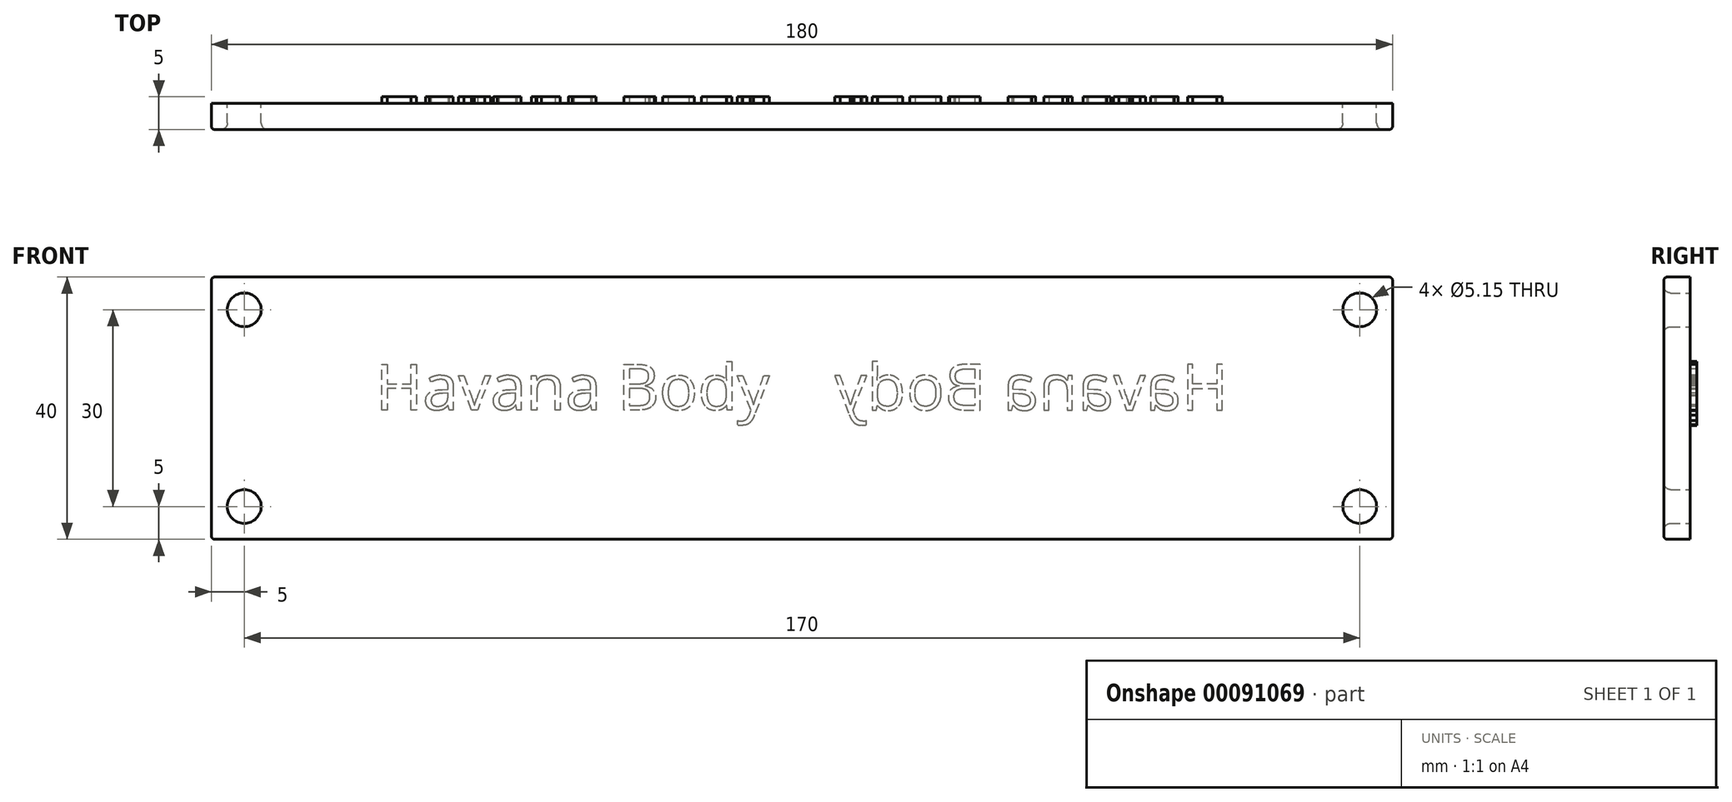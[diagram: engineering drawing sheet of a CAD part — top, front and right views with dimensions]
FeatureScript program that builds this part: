
annotation { "Feature Type Name" : "Feature", "Feature Type Description" : "" }
export const myFeature = defineFeature(function(context is Context, id is Id, definition is map)
    precondition{}
    {
        {
            var Q0;
            Q0=qCreatedBy(makeId("Front.planeOp"),FACE);
            var sketch = newSketch(context, id + "F0", { "sketchPlane" : qUnion([Q0])});
            skLineSegment(sketch, "E0.bottom", {"start": v(-90, -20) * mm, "end": v(90, -20) * mm});
            skLineSegment(sketch, "E0.top", {"start": v(-90, 20) * mm, "end": v(90, 20) * mm});
            skLineSegment(sketch, "E0.left", {"start": v(-90, -20) * mm, "end": v(-90, 20) * mm});
            skLineSegment(sketch, "E0.right", {"start": v(90, -20) * mm, "end": v(90, 20) * mm});
            skPoint(sketch, "E0.middle", {"position": v(0, 0) * mm});
            skCircle(sketch, "E1", {"center": v(-85, 15) * mm, "radius": 2.58 * mm});
            skPoint(sketch, "E2.start.orphan", {"position": v(-90, 0) * mm});
            skPoint(sketch, "E3.orphan", {"position": v(0, 20) * mm});
            skPoint(sketch, "E4.end.orphan", {"position": v(0, -20) * mm});
            skLineSegment(sketch, "E5", {"start": v(-90, 0) * mm, "end": v(0, 0) * mm, "construction": true});
            skLineSegment(sketch, "E6", {"start": v(0, 20) * mm, "end": v(0, -20) * mm, "construction": true});
            skCircle(sketch, "E7.MirrorC", {"center": v(-85, -15) * mm, "radius": 2.58 * mm});
            skCircle(sketch, "E8.MirrorC", {"center": v(85, 15) * mm, "radius": 2.58 * mm});
            skCircle(sketch, "E9.MirrorC", {"center": v(85, -15) * mm, "radius": 2.58 * mm});
            skSolve(sketch);
        }
        {
            var Q0;
            Q0=makeQuery(id+"F0.imprint","IMPRINT",FACE,{"disambiguationData":[TD([[makeQuery(id+"F0.imprint","IMPRINT",EDGE,{"derivedFrom":sQuery(id+"F0.wireOp",EDGE,"E0.bottom")}),1.0]])]});
            extrude(context, id + "F1", {"entities" : qUnion([Q0]), "depth" : 4 * mm});
        }
        {
            var Q0;
            Q0=makeQuery(id+"F1.opExtrude","CAP_EDGE",EDGE,{"disambiguationData":[OSD([sQuery(id+"F0.wireOp",EDGE,"E1")])],"isStart":false});
            var Q1;
            Q1=makeQuery(id+"F1.opExtrude","CAP_EDGE",EDGE,{"disambiguationData":[OSD([sQuery(id+"F0.wireOp",EDGE,"f5b72a5b-8583-449a-bdbf-9ac5a681e1fd0.MirrorC")])],"isStart":false});
            var Q2;
            Q2=makeQuery(id+"F1.opExtrude","CAP_EDGE",EDGE,{"disambiguationData":[OSD([sQuery(id+"F0.wireOp",EDGE,"2623e306-60f4-4522-aa65-1e3e8c2cf5b60.MirrorC")])],"isStart":false});
            var Q3;
            Q3=makeQuery(id+"F1.opExtrude","CAP_EDGE",EDGE,{"disambiguationData":[OSD([sQuery(id+"F0.wireOp",EDGE,"be81a34d-1d50-4ce7-a7a8-4484a1701fac0.MirrorC")])],"isStart":false});
            var Q4;
            Q4=makeQuery(id+"F1.opExtrude","CAP_EDGE",EDGE,{"disambiguationData":[OSD([sQuery(id+"F0.wireOp",EDGE,"E7.MirrorC")])],"isStart":false});
            var Q5;
            Q5=makeQuery(id+"F1.opExtrude","CAP_EDGE",EDGE,{"disambiguationData":[OSD([sQuery(id+"F0.wireOp",EDGE,"E8.MirrorC")])],"isStart":false});
            var Q6;
            Q6=makeQuery(id+"F1.opExtrude","CAP_EDGE",EDGE,{"disambiguationData":[OSD([sQuery(id+"F0.wireOp",EDGE,"E9.MirrorC")])],"isStart":false});
            fillet(context, id + "F2", {"entities" : qUnion([Q0, Q1, Q2, Q3, Q4, Q5, Q6]), "radius" : 1 * mm, "tangentPropagation" : true, "allowEdgeOverflow" : false});
        }
        {
            var Q0;
            Q0=makeQuery(id+"F1.opExtrude","CAP_EDGE",EDGE,{"disambiguationData":[OSD([sQuery(id+"F0.wireOp",EDGE,"E0.top")])],"isStart":false});
            var Q1;
            Q1=makeQuery(id+"F1.opExtrude","CAP_EDGE",EDGE,{"disambiguationData":[OSD([sQuery(id+"F0.wireOp",EDGE,"E0.left")])],"isStart":false});
            var Q2;
            Q2=makeQuery(id+"F1.opExtrude","CAP_EDGE",EDGE,{"disambiguationData":[OSD([sQuery(id+"F0.wireOp",EDGE,"E0.bottom")])],"isStart":false});
            var Q3;
            Q3=makeQuery(id+"F1.opExtrude","CAP_EDGE",EDGE,{"disambiguationData":[OSD([sQuery(id+"F0.wireOp",EDGE,"E0.right")])],"isStart":false});
            var Q4;
            Q4=makeQuery(id+"F1.opExtrude","SWEPT_EDGE",EDGE,{"disambiguationData":[OSD([sQuery(id+"F0.wireOp",EDGE,"E0.top"),sQuery(id+"F0.wireOp",EDGE,"E0.left")])]});
            var Q5;
            Q5=makeQuery(id+"F1.opExtrude","SWEPT_EDGE",EDGE,{"disambiguationData":[OSD([sQuery(id+"F0.wireOp",EDGE,"E0.bottom"),sQuery(id+"F0.wireOp",EDGE,"E0.left")])]});
            var Q6;
            Q6=makeQuery(id+"F1.opExtrude","SWEPT_EDGE",EDGE,{"disambiguationData":[OSD([sQuery(id+"F0.wireOp",EDGE,"E0.top"),sQuery(id+"F0.wireOp",EDGE,"E0.right")])]});
            var Q7;
            Q7=makeQuery(id+"F1.opExtrude","SWEPT_EDGE",EDGE,{"disambiguationData":[OSD([sQuery(id+"F0.wireOp",EDGE,"E0.bottom"),sQuery(id+"F0.wireOp",EDGE,"E0.right")])]});
            fillet(context, id + "F3", {"entities" : qUnion([Q0, Q1, Q2, Q3, Q4, Q5, Q6, Q7]), "radius" : .5 * mm, "tangentPropagation" : true, "allowEdgeOverflow" : false});
        }
        {
            var Q0;
            Q0=makeQuery(id+"F1.opExtrude","CAP_FACE",FACE,{"disambiguationData":[OSD([sQuery(id+"F0.wireOp",EDGE,"E0.bottom"),sQuery(id+"F0.wireOp",EDGE,"E0.top"),sQuery(id+"F0.wireOp",EDGE,"E0.left"),sQuery(id+"F0.wireOp",EDGE,"E0.right"),sQuery(id+"F0.wireOp",EDGE,"E1"),sQuery(id+"F0.wireOp",EDGE,"E7.MirrorC"),sQuery(id+"F0.wireOp",EDGE,"E8.MirrorC"),sQuery(id+"F0.wireOp",EDGE,"E9.MirrorC")])],"isStart":true});
            var sketch = newSketch(context, id + "F4", { "sketchPlane" : qUnion([Q0])});
            skText(sketch, "E10", { "text": "Havana Body", "fontName": "OpenSans-Regular.ttf"});
            skLineSegment(sketch, "E11", {"start": v(0, 20) * mm, "end": v(0, -20) * mm, "construction": true});
            const initialGuessF4  = {"E10": [-0.065, -0.00027, 1, 0, 0.00703]};
            skSetInitialGuess(sketch, initialGuessF4);
            skSolve(sketch);
        }
        {
            var Q0;
            Q0=qSketchRegion(id+"F4",true);
            extrude(context, id + "F5", {"entities" : qUnion([Q0]), "operationType" : NewBodyOperationType.ADD, "depth" : 1 * mm});
        }
        {
            var Q0;
            Q0=makeQuery(id+"F1.opExtrude","SWEPT_BODY",BODY,{"disambiguationData":[OSD([sQuery(id+"F0.wireOp",EDGE,"E0.bottom"),sQuery(id+"F0.wireOp",EDGE,"E0.top"),sQuery(id+"F0.wireOp",EDGE,"E0.left"),sQuery(id+"F0.wireOp",EDGE,"E0.right"),sQuery(id+"F0.wireOp",EDGE,"E1"),sQuery(id+"F0.wireOp",EDGE,"E7.MirrorC"),sQuery(id+"F0.wireOp",EDGE,"E8.MirrorC"),sQuery(id+"F0.wireOp",EDGE,"E9.MirrorC")])]});
            var Q1;
            Q1=makeQuery(id+"F5.opExtrude","SWEPT_FACE",FACE,{"disambiguationData":[OSD([sQuery(id+"F4.wireOp",EDGE,"E10.sketch_text.stroke-94")])]});
            var Q2;
            Q2=makeQuery(id+"F5.opExtrude","SWEPT_FACE",FACE,{"disambiguationData":[OSD([sQuery(id+"F4.wireOp",EDGE,"E10.sketch_text.stroke-169")])]});
            var Q3;
            Q3=makeQuery(id+"F5.opExtrude","SWEPT_FACE",FACE,{"disambiguationData":[OSD([sQuery(id+"F4.wireOp",EDGE,"E10.sketch_text.stroke-185")])]});
            var Q4;
            Q4=makeQuery(id+"F5.opExtrude","SWEPT_FACE",FACE,{"disambiguationData":[OSD([sQuery(id+"F4.wireOp",EDGE,"E10.sketch_text.stroke-125")])]});
            var Q5;
            Q5=makeQuery(id+"F5.opExtrude","SWEPT_FACE",FACE,{"disambiguationData":[OSD([sQuery(id+"F4.wireOp",EDGE,"E10.sketch_text.stroke-155")])]});
            var Q6;
            Q6=makeQuery(id+"F5.opExtrude","SWEPT_FACE",FACE,{"disambiguationData":[OSD([sQuery(id+"F4.wireOp",EDGE,"E10.sketch_text.stroke-65")])]});
            var Q7;
            Q7=makeQuery(id+"F5.opExtrude","SWEPT_FACE",FACE,{"disambiguationData":[OSD([sQuery(id+"F4.wireOp",EDGE,"E10.sketch_text.stroke-81")])]});
            var Q8;
            Q8=makeQuery(id+"F5.opExtrude","SWEPT_FACE",FACE,{"disambiguationData":[OSD([sQuery(id+"F4.wireOp",EDGE,"E10.sketch_text.stroke-67")])]});
            var Q9;
            Q9=makeQuery(id+"F5.opExtrude","SWEPT_FACE",FACE,{"disambiguationData":[OSD([sQuery(id+"F4.wireOp",EDGE,"E10.sketch_text.stroke-99")])]});
            var Q10;
            Q10=makeQuery(id+"F5.opExtrude","SWEPT_FACE",FACE,{"disambiguationData":[OSD([sQuery(id+"F4.wireOp",EDGE,"E10.sketch_text.stroke-127")])]});
            var Q11;
            Q11=makeQuery(id+"F5.opExtrude","SWEPT_FACE",FACE,{"disambiguationData":[OSD([sQuery(id+"F4.wireOp",EDGE,"E10.sketch_text.stroke-10")])]});
            var Q12;
            Q12=makeQuery(id+"F5.opExtrude","CAP_FACE",FACE,{"disambiguationData":[OSD([sQuery(id+"F4.wireOp",EDGE,"E10.sketch_text.stroke-9"),sQuery(id+"F4.wireOp",EDGE,"E10.sketch_text.stroke-10"),sQuery(id+"F4.wireOp",EDGE,"E10.sketch_text.stroke-11"),sQuery(id+"F4.wireOp",EDGE,"E10.sketch_text.stroke-12")])],"isStart":false});
            var Q13;
            Q13=makeQuery(id+"F5.opExtrude","SWEPT_FACE",FACE,{"disambiguationData":[OSD([sQuery(id+"F4.wireOp",EDGE,"E10.sketch_text.stroke-154")])]});
            var Q14;
            Q14=makeQuery(id+"F5.opExtrude","SWEPT_FACE",FACE,{"disambiguationData":[OSD([sQuery(id+"F4.wireOp",EDGE,"E10.sketch_text.stroke-1")])]});
            var Q15;
            Q15=makeQuery(id+"F5.opExtrude","CAP_FACE",FACE,{"disambiguationData":[OSD([sQuery(id+"F4.wireOp",EDGE,"E10.sketch_text.stroke-124"),sQuery(id+"F4.wireOp",EDGE,"E10.sketch_text.stroke-125"),sQuery(id+"F4.wireOp",EDGE,"E10.sketch_text.stroke-126"),sQuery(id+"F4.wireOp",EDGE,"E10.sketch_text.stroke-127"),sQuery(id+"F4.wireOp",EDGE,"E10.sketch_text.stroke-128"),sQuery(id+"F4.wireOp",EDGE,"E10.sketch_text.stroke-129"),sQuery(id+"F4.wireOp",EDGE,"E10.sketch_text.stroke-130"),sQuery(id+"F4.wireOp",EDGE,"E10.sketch_text.stroke-131"),sQuery(id+"F4.wireOp",EDGE,"E10.sketch_text.stroke-132"),sQuery(id+"F4.wireOp",EDGE,"E10.sketch_text.stroke-133"),sQuery(id+"F4.wireOp",EDGE,"E10.sketch_text.stroke-134"),sQuery(id+"F4.wireOp",EDGE,"E10.sketch_text.stroke-135"),sQuery(id+"F4.wireOp",EDGE,"E10.sketch_text.stroke-136"),sQuery(id+"F4.wireOp",EDGE,"E10.sketch_text.stroke-137"),sQuery(id+"F4.wireOp",EDGE,"E10.sketch_text.stroke-138")])],"isStart":false});
            var Q16;
            Q16=makeQuery(id+"F5.opExtrude","CAP_FACE",FACE,{"disambiguationData":[OSD([sQuery(id+"F4.wireOp",EDGE,"E10.sketch_text.stroke-34"),sQuery(id+"F4.wireOp",EDGE,"E10.sketch_text.stroke-35"),sQuery(id+"F4.wireOp",EDGE,"E10.sketch_text.stroke-36"),sQuery(id+"F4.wireOp",EDGE,"E10.sketch_text.stroke-37"),sQuery(id+"F4.wireOp",EDGE,"E10.sketch_text.stroke-38"),sQuery(id+"F4.wireOp",EDGE,"E10.sketch_text.stroke-39"),sQuery(id+"F4.wireOp",EDGE,"E10.sketch_text.stroke-40"),sQuery(id+"F4.wireOp",EDGE,"E10.sketch_text.stroke-41"),sQuery(id+"F4.wireOp",EDGE,"E10.sketch_text.stroke-42"),sQuery(id+"F4.wireOp",EDGE,"E10.sketch_text.stroke-43"),sQuery(id+"F4.wireOp",EDGE,"E10.sketch_text.stroke-44"),sQuery(id+"F4.wireOp",EDGE,"E10.sketch_text.stroke-45"),sQuery(id+"F4.wireOp",EDGE,"E10.sketch_text.stroke-46"),sQuery(id+"F4.wireOp",EDGE,"E10.sketch_text.stroke-47"),sQuery(id+"F4.wireOp",EDGE,"E10.sketch_text.stroke-48"),sQuery(id+"F4.wireOp",EDGE,"E10.sketch_text.stroke-49"),sQuery(id+"F4.wireOp",EDGE,"E10.sketch_text.stroke-50"),sQuery(id+"F4.wireOp",EDGE,"E10.sketch_text.stroke-51"),sQuery(id+"F4.wireOp",EDGE,"E10.sketch_text.stroke-52"),sQuery(id+"F4.wireOp",EDGE,"E10.sketch_text.stroke-53"),sQuery(id+"F4.wireOp",EDGE,"E10.sketch_text.stroke-54"),sQuery(id+"F4.wireOp",EDGE,"E10.sketch_text.stroke-55"),sQuery(id+"F4.wireOp",EDGE,"E10.sketch_text.stroke-56"),sQuery(id+"F4.wireOp",EDGE,"E10.sketch_text.stroke-57"),sQuery(id+"F4.wireOp",EDGE,"E10.sketch_text.stroke-58"),sQuery(id+"F4.wireOp",EDGE,"E10.sketch_text.stroke-59"),sQuery(id+"F4.wireOp",EDGE,"E10.sketch_text.stroke-60")])],"isStart":false});
            var Q17;
            Q17=makeQuery(id+"F5.opExtrude","SWEPT_FACE",FACE,{"disambiguationData":[OSD([sQuery(id+"F4.wireOp",EDGE,"E10.sketch_text.stroke-50")])]});
            var Q18;
            Q18=makeQuery(id+"F5.opExtrude","SWEPT_FACE",FACE,{"disambiguationData":[OSD([sQuery(id+"F4.wireOp",EDGE,"E10.sketch_text.stroke-2")])]});
            var Q19;
            Q19=makeQuery(id+"F5.opExtrude","SWEPT_FACE",FACE,{"disambiguationData":[OSD([sQuery(id+"F4.wireOp",EDGE,"E10.sketch_text.stroke-3")])]});
            var Q20;
            Q20=makeQuery(id+"F5.opExtrude","SWEPT_FACE",FACE,{"disambiguationData":[OSD([sQuery(id+"F4.wireOp",EDGE,"E10.sketch_text.stroke-5")])]});
            var Q21;
            Q21=makeQuery(id+"F5.opExtrude","SWEPT_FACE",FACE,{"disambiguationData":[OSD([sQuery(id+"F4.wireOp",EDGE,"E10.sketch_text.stroke-8")])]});
            var Q22;
            Q22=makeQuery(id+"F5.opExtrude","SWEPT_FACE",FACE,{"disambiguationData":[OSD([sQuery(id+"F4.wireOp",EDGE,"E10.sketch_text.stroke-98")])]});
            var Q23;
            Q23=makeQuery(id+"F5.opExtrude","SWEPT_FACE",FACE,{"disambiguationData":[OSD([sQuery(id+"F4.wireOp",EDGE,"E10.sketch_text.stroke-66")])]});
            var Q24;
            Q24=makeQuery(id+"F5.opExtrude","SWEPT_FACE",FACE,{"disambiguationData":[OSD([sQuery(id+"F4.wireOp",EDGE,"E10.sketch_text.stroke-153")])]});
            var Q25;
            Q25=makeQuery(id+"F5.opExtrude","SWEPT_FACE",FACE,{"disambiguationData":[OSD([sQuery(id+"F4.wireOp",EDGE,"E10.sketch_text.stroke-126")])]});
            var Q26;
            Q26=makeQuery(id+"F5.opExtrude","SWEPT_FACE",FACE,{"disambiguationData":[OSD([sQuery(id+"F4.wireOp",EDGE,"E10.sketch_text.stroke-183")])]});
            var Q27;
            Q27=makeQuery(id+"F5.opExtrude","SWEPT_FACE",FACE,{"disambiguationData":[OSD([sQuery(id+"F4.wireOp",EDGE,"E10.sketch_text.stroke-109")])]});
            var Q28;
            Q28=makeQuery(id+"F5.opExtrude","SWEPT_FACE",FACE,{"disambiguationData":[OSD([sQuery(id+"F4.wireOp",EDGE,"E10.sketch_text.stroke-186")])]});
            var Q29;
            Q29=makeQuery(id+"F5.opExtrude","SWEPT_FACE",FACE,{"disambiguationData":[OSD([sQuery(id+"F4.wireOp",EDGE,"E10.sketch_text.stroke-79")])]});
            var Q30;
            Q30=makeQuery(id+"F5.opExtrude","SWEPT_FACE",FACE,{"disambiguationData":[OSD([sQuery(id+"F4.wireOp",EDGE,"E10.sketch_text.stroke-110")])]});
            var Q31;
            Q31=makeQuery(id+"F5.opExtrude","SWEPT_FACE",FACE,{"disambiguationData":[OSD([sQuery(id+"F4.wireOp",EDGE,"E10.sketch_text.stroke-38")])]});
            var Q32;
            Q32=makeQuery(id+"F5.opExtrude","SWEPT_FACE",FACE,{"disambiguationData":[OSD([sQuery(id+"F4.wireOp",EDGE,"E10.sketch_text.stroke-24")])]});
            var Q33;
            Q33=makeQuery(id+"F5.opExtrude","SWEPT_FACE",FACE,{"disambiguationData":[OSD([sQuery(id+"F4.wireOp",EDGE,"E10.sketch_text.stroke-12")])]});
            var Q34;
            Q34=makeQuery(id+"F5.opExtrude","SWEPT_FACE",FACE,{"disambiguationData":[OSD([sQuery(id+"F4.wireOp",EDGE,"E10.sketch_text.stroke-100")])]});
            var Q35;
            Q35=makeQuery(id+"F5.opExtrude","SWEPT_FACE",FACE,{"disambiguationData":[OSD([sQuery(id+"F4.wireOp",EDGE,"E10.sketch_text.stroke-158")])]});
            var Q36;
            Q36=makeQuery(id+"F5.opExtrude","SWEPT_FACE",FACE,{"disambiguationData":[OSD([sQuery(id+"F4.wireOp",EDGE,"E10.sketch_text.stroke-142")])]});
            var Q37;
            Q37=makeQuery(id+"F5.opExtrude","SWEPT_FACE",FACE,{"disambiguationData":[OSD([sQuery(id+"F4.wireOp",EDGE,"E10.sketch_text.stroke-54")])]});
            var Q38;
            Q38=makeQuery(id+"F5.opExtrude","SWEPT_FACE",FACE,{"disambiguationData":[OSD([sQuery(id+"F4.wireOp",EDGE,"E10.sketch_text.stroke-25")])]});
            var Q39;
            Q39=makeQuery(id+"F5.opExtrude","SWEPT_FACE",FACE,{"disambiguationData":[OSD([sQuery(id+"F4.wireOp",EDGE,"E10.sketch_text.stroke-101")])]});
            var Q40;
            Q40=makeQuery(id+"F5.opExtrude","SWEPT_FACE",FACE,{"disambiguationData":[OSD([sQuery(id+"F4.wireOp",EDGE,"E10.sketch_text.stroke-69")])]});
            var Q41;
            Q41=makeQuery(id+"F5.opExtrude","SWEPT_FACE",FACE,{"disambiguationData":[OSD([sQuery(id+"F4.wireOp",EDGE,"E10.sketch_text.stroke-159")])]});
            var Q42;
            Q42=makeQuery(id+"F5.opExtrude","SWEPT_FACE",FACE,{"disambiguationData":[OSD([sQuery(id+"F4.wireOp",EDGE,"E10.sketch_text.stroke-85")])]});
            var Q43;
            Q43=makeQuery(id+"F5.opExtrude","SWEPT_FACE",FACE,{"disambiguationData":[OSD([sQuery(id+"F4.wireOp",EDGE,"E10.sketch_text.stroke-173")])]});
            var Q44;
            Q44=makeQuery(id+"F5.opExtrude","SWEPT_FACE",FACE,{"disambiguationData":[OSD([sQuery(id+"F4.wireOp",EDGE,"E10.sketch_text.stroke-40")])]});
            var Q45;
            Q45=makeQuery(id+"F5.opExtrude","SWEPT_FACE",FACE,{"disambiguationData":[OSD([sQuery(id+"F4.wireOp",EDGE,"E10.sketch_text.stroke-102")])]});
            var Q46;
            Q46=makeQuery(id+"F5.opExtrude","SWEPT_FACE",FACE,{"disambiguationData":[OSD([sQuery(id+"F4.wireOp",EDGE,"E10.sketch_text.stroke-86")])]});
            var Q47;
            Q47=makeQuery(id+"F5.opExtrude","SWEPT_FACE",FACE,{"disambiguationData":[OSD([sQuery(id+"F4.wireOp",EDGE,"E10.sketch_text.stroke-130")])]});
            var Q48;
            Q48=makeQuery(id+"F5.opExtrude","SWEPT_FACE",FACE,{"disambiguationData":[OSD([sQuery(id+"F4.wireOp",EDGE,"E10.sketch_text.stroke-103")])]});
            var Q49;
            Q49=makeQuery(id+"F5.opExtrude","SWEPT_FACE",FACE,{"disambiguationData":[OSD([sQuery(id+"F4.wireOp",EDGE,"E10.sketch_text.stroke-87")])]});
            var Q50;
            Q50=makeQuery(id+"F5.opExtrude","SWEPT_FACE",FACE,{"disambiguationData":[OSD([sQuery(id+"F4.wireOp",EDGE,"E10.sketch_text.stroke-145")])]});
            var Q51;
            Q51=makeQuery(id+"F5.opExtrude","SWEPT_FACE",FACE,{"disambiguationData":[OSD([sQuery(id+"F4.wireOp",EDGE,"E10.sketch_text.stroke-131")])]});
            var Q52;
            Q52=makeQuery(id+"F5.opExtrude","SWEPT_FACE",FACE,{"disambiguationData":[OSD([sQuery(id+"F4.wireOp",EDGE,"E10.sketch_text.stroke-28")])]});
            var Q53;
            Q53=makeQuery(id+"F5.opExtrude","SWEPT_FACE",FACE,{"disambiguationData":[OSD([sQuery(id+"F4.wireOp",EDGE,"E10.sketch_text.stroke-14")])]});
            var Q54;
            Q54=makeQuery(id+"F5.opExtrude","SWEPT_FACE",FACE,{"disambiguationData":[OSD([sQuery(id+"F4.wireOp",EDGE,"E10.sketch_text.stroke-88")])]});
            var Q55;
            Q55=makeQuery(id+"F5.opExtrude","SWEPT_FACE",FACE,{"disambiguationData":[OSD([sQuery(id+"F4.wireOp",EDGE,"E10.sketch_text.stroke-162")])]});
            var Q56;
            Q56=makeQuery(id+"F5.opExtrude","SWEPT_FACE",FACE,{"disambiguationData":[OSD([sQuery(id+"F4.wireOp",EDGE,"E10.sketch_text.stroke-176")])]});
            var Q57;
            Q57=makeQuery(id+"F5.opExtrude","SWEPT_FACE",FACE,{"disambiguationData":[OSD([sQuery(id+"F4.wireOp",EDGE,"E10.sketch_text.stroke-73")])]});
            var Q58;
            Q58=makeQuery(id+"F5.opExtrude","SWEPT_FACE",FACE,{"disambiguationData":[OSD([sQuery(id+"F4.wireOp",EDGE,"E10.sketch_text.stroke-59")])]});
            var Q59;
            Q59=makeQuery(id+"F5.opExtrude","SWEPT_FACE",FACE,{"disambiguationData":[OSD([sQuery(id+"F4.wireOp",EDGE,"E10.sketch_text.stroke-133")])]});
            var Q60;
            Q60=makeQuery(id+"F5.opExtrude","SWEPT_FACE",FACE,{"disambiguationData":[OSD([sQuery(id+"F4.wireOp",EDGE,"E10.sketch_text.stroke-119")])]});
            var Q61;
            Q61=makeQuery(id+"F5.opExtrude","SWEPT_FACE",FACE,{"disambiguationData":[OSD([sQuery(id+"F4.wireOp",EDGE,"E10.sketch_text.stroke-74")])]});
            var Q62;
            Q62=makeQuery(id+"F5.opExtrude","SWEPT_FACE",FACE,{"disambiguationData":[OSD([sQuery(id+"F4.wireOp",EDGE,"E10.sketch_text.stroke-44")])]});
            var Q63;
            Q63=makeQuery(id+"F5.opExtrude","SWEPT_FACE",FACE,{"disambiguationData":[OSD([sQuery(id+"F4.wireOp",EDGE,"E10.sketch_text.stroke-120")])]});
            var Q64;
            Q64=makeQuery(id+"F5.opExtrude","SWEPT_FACE",FACE,{"disambiguationData":[OSD([sQuery(id+"F4.wireOp",EDGE,"E10.sketch_text.stroke-90")])]});
            var Q65;
            Q65=makeQuery(id+"F5.opExtrude","SWEPT_FACE",FACE,{"disambiguationData":[OSD([sQuery(id+"F4.wireOp",EDGE,"E10.sketch_text.stroke-178")])]});
            var Q66;
            Q66=makeQuery(id+"F5.opExtrude","SWEPT_FACE",FACE,{"disambiguationData":[OSD([sQuery(id+"F4.wireOp",EDGE,"E10.sketch_text.stroke-45")])]});
            var Q67;
            Q67=makeQuery(id+"F5.opExtrude","SWEPT_FACE",FACE,{"disambiguationData":[OSD([sQuery(id+"F4.wireOp",EDGE,"E10.sketch_text.stroke-31")])]});
            var Q68;
            Q68=makeQuery(id+"F5.opExtrude","SWEPT_FACE",FACE,{"disambiguationData":[OSD([sQuery(id+"F4.wireOp",EDGE,"E10.sketch_text.stroke-135")])]});
            var Q69;
            Q69=makeQuery(id+"F5.opExtrude","SWEPT_FACE",FACE,{"disambiguationData":[OSD([sQuery(id+"F4.wireOp",EDGE,"E10.sketch_text.stroke-179")])]});
            var Q70;
            Q70=makeQuery(id+"F5.opExtrude","SWEPT_FACE",FACE,{"disambiguationData":[OSD([sQuery(id+"F4.wireOp",EDGE,"E10.sketch_text.stroke-165")])]});
            var Q71;
            Q71=makeQuery(id+"F5.opExtrude","SWEPT_FACE",FACE,{"disambiguationData":[OSD([sQuery(id+"F4.wireOp",EDGE,"E10.sketch_text.stroke-149")])]});
            var Q72;
            Q72=makeQuery(id+"F5.opExtrude","SWEPT_FACE",FACE,{"disambiguationData":[OSD([sQuery(id+"F4.wireOp",EDGE,"E10.sketch_text.stroke-136")])]});
            var Q73;
            Q73=makeQuery(id+"F5.opExtrude","SWEPT_FACE",FACE,{"disambiguationData":[OSD([sQuery(id+"F4.wireOp",EDGE,"E10.sketch_text.stroke-122")])]});
            var Q74;
            Q74=makeQuery(id+"F5.opExtrude","SWEPT_FACE",FACE,{"disambiguationData":[OSD([sQuery(id+"F4.wireOp",EDGE,"E10.sketch_text.stroke-106")])]});
            var Q75;
            Q75=makeQuery(id+"F5.opExtrude","SWEPT_FACE",FACE,{"disambiguationData":[OSD([sQuery(id+"F4.wireOp",EDGE,"E10.sketch_text.stroke-180")])]});
            var Q76;
            Q76=makeQuery(id+"F5.opExtrude","SWEPT_FACE",FACE,{"disambiguationData":[OSD([sQuery(id+"F4.wireOp",EDGE,"E10.sketch_text.stroke-166")])]});
            var Q77;
            Q77=makeQuery(id+"F5.opExtrude","SWEPT_FACE",FACE,{"disambiguationData":[OSD([sQuery(id+"F4.wireOp",EDGE,"E10.sketch_text.stroke-150")])]});
            var Q78;
            Q78=makeQuery(id+"F5.opExtrude","SWEPT_FACE",FACE,{"disambiguationData":[OSD([sQuery(id+"F4.wireOp",EDGE,"E10.sketch_text.stroke-76")])]});
            var Q79;
            Q79=makeQuery(id+"F5.opExtrude","SWEPT_FACE",FACE,{"disambiguationData":[OSD([sQuery(id+"F4.wireOp",EDGE,"E10.sketch_text.stroke-32")])]});
            var Q80;
            Q80=makeQuery(id+"F5.opExtrude","SWEPT_FACE",FACE,{"disambiguationData":[OSD([sQuery(id+"F4.wireOp",EDGE,"E10.sketch_text.stroke-181")])]});
            var Q81;
            Q81=makeQuery(id+"F5.opExtrude","SWEPT_FACE",FACE,{"disambiguationData":[OSD([sQuery(id+"F4.wireOp",EDGE,"E10.sketch_text.stroke-47")])]});
            var Q82;
            Q82=makeQuery(id+"F5.opExtrude","SWEPT_FACE",FACE,{"disambiguationData":[OSD([sQuery(id+"F4.wireOp",EDGE,"E10.sketch_text.stroke-123")])]});
            var Q83;
            Q83=makeQuery(id+"F5.opExtrude","SWEPT_FACE",FACE,{"disambiguationData":[OSD([sQuery(id+"F4.wireOp",EDGE,"E10.sketch_text.stroke-107")])]});
            var Q84;
            Q84=makeQuery(id+"F5.opExtrude","SWEPT_FACE",FACE,{"disambiguationData":[OSD([sQuery(id+"F4.wireOp",EDGE,"E10.sketch_text.stroke-48")])]});
            var Q85;
            Q85=makeQuery(id+"F5.opExtrude","SWEPT_FACE",FACE,{"disambiguationData":[OSD([sQuery(id+"F4.wireOp",EDGE,"E10.sketch_text.stroke-124")])]});
            var Q86;
            Q86=makeQuery(id+"F5.opExtrude","SWEPT_FACE",FACE,{"disambiguationData":[OSD([sQuery(id+"F4.wireOp",EDGE,"E10.sketch_text.stroke-108")])]});
            var Q87;
            Q87=makeQuery(id+"F5.opExtrude","CAP_FACE",FACE,{"disambiguationData":[OSD([sQuery(id+"F4.wireOp",EDGE,"E10.sketch_text.stroke-139"),sQuery(id+"F4.wireOp",EDGE,"E10.sketch_text.stroke-140"),sQuery(id+"F4.wireOp",EDGE,"E10.sketch_text.stroke-141"),sQuery(id+"F4.wireOp",EDGE,"E10.sketch_text.stroke-142"),sQuery(id+"F4.wireOp",EDGE,"E10.sketch_text.stroke-143"),sQuery(id+"F4.wireOp",EDGE,"E10.sketch_text.stroke-144"),sQuery(id+"F4.wireOp",EDGE,"E10.sketch_text.stroke-145"),sQuery(id+"F4.wireOp",EDGE,"E10.sketch_text.stroke-146"),sQuery(id+"F4.wireOp",EDGE,"E10.sketch_text.stroke-147"),sQuery(id+"F4.wireOp",EDGE,"E10.sketch_text.stroke-148"),sQuery(id+"F4.wireOp",EDGE,"E10.sketch_text.stroke-149"),sQuery(id+"F4.wireOp",EDGE,"E10.sketch_text.stroke-150"),sQuery(id+"F4.wireOp",EDGE,"E10.sketch_text.stroke-151"),sQuery(id+"F4.wireOp",EDGE,"E10.sketch_text.stroke-152"),sQuery(id+"F4.wireOp",EDGE,"E10.sketch_text.stroke-153"),sQuery(id+"F4.wireOp",EDGE,"E10.sketch_text.stroke-154"),sQuery(id+"F4.wireOp",EDGE,"E10.sketch_text.stroke-155"),sQuery(id+"F4.wireOp",EDGE,"E10.sketch_text.stroke-156"),sQuery(id+"F4.wireOp",EDGE,"E10.sketch_text.stroke-157"),sQuery(id+"F4.wireOp",EDGE,"E10.sketch_text.stroke-158"),sQuery(id+"F4.wireOp",EDGE,"E10.sketch_text.stroke-159"),sQuery(id+"F4.wireOp",EDGE,"E10.sketch_text.stroke-160"),sQuery(id+"F4.wireOp",EDGE,"E10.sketch_text.stroke-161"),sQuery(id+"F4.wireOp",EDGE,"E10.sketch_text.stroke-162"),sQuery(id+"F4.wireOp",EDGE,"E10.sketch_text.stroke-163"),sQuery(id+"F4.wireOp",EDGE,"E10.sketch_text.stroke-164"),sQuery(id+"F4.wireOp",EDGE,"E10.sketch_text.stroke-165")])],"isStart":false});
            var Q88;
            Q88=makeQuery(id+"F5.opExtrude","CAP_FACE",FACE,{"disambiguationData":[OSD([sQuery(id+"F4.wireOp",EDGE,"E10.sketch_text.stroke-21"),sQuery(id+"F4.wireOp",EDGE,"E10.sketch_text.stroke-22"),sQuery(id+"F4.wireOp",EDGE,"E10.sketch_text.stroke-23"),sQuery(id+"F4.wireOp",EDGE,"E10.sketch_text.stroke-24"),sQuery(id+"F4.wireOp",EDGE,"E10.sketch_text.stroke-25"),sQuery(id+"F4.wireOp",EDGE,"E10.sketch_text.stroke-26"),sQuery(id+"F4.wireOp",EDGE,"E10.sketch_text.stroke-27"),sQuery(id+"F4.wireOp",EDGE,"E10.sketch_text.stroke-28"),sQuery(id+"F4.wireOp",EDGE,"E10.sketch_text.stroke-29"),sQuery(id+"F4.wireOp",EDGE,"E10.sketch_text.stroke-30"),sQuery(id+"F4.wireOp",EDGE,"E10.sketch_text.stroke-31"),sQuery(id+"F4.wireOp",EDGE,"E10.sketch_text.stroke-32"),sQuery(id+"F4.wireOp",EDGE,"E10.sketch_text.stroke-33")])],"isStart":false});
            var Q89;
            Q89=makeQuery(id+"F5.opExtrude","SWEPT_FACE",FACE,{"disambiguationData":[OSD([sQuery(id+"F4.wireOp",EDGE,"E10.sketch_text.stroke-113")])]});
            var Q90;
            Q90=makeQuery(id+"F5.opExtrude","SWEPT_FACE",FACE,{"disambiguationData":[OSD([sQuery(id+"F4.wireOp",EDGE,"E10.sketch_text.stroke-37")])]});
            var Q91;
            Q91=makeQuery(id+"F5.opExtrude","SWEPT_FACE",FACE,{"disambiguationData":[OSD([sQuery(id+"F4.wireOp",EDGE,"E10.sketch_text.stroke-187")])]});
            var Q92;
            Q92=makeQuery(id+"F5.opExtrude","SWEPT_FACE",FACE,{"disambiguationData":[OSD([sQuery(id+"F4.wireOp",EDGE,"E10.sketch_text.stroke-0")])]});
            var Q93;
            Q93=makeQuery(id+"F5.opExtrude","SWEPT_FACE",FACE,{"disambiguationData":[OSD([sQuery(id+"F4.wireOp",EDGE,"E10.sketch_text.stroke-4")])]});
            var Q94;
            Q94=makeQuery(id+"F5.opExtrude","SWEPT_FACE",FACE,{"disambiguationData":[OSD([sQuery(id+"F4.wireOp",EDGE,"E10.sketch_text.stroke-82")])]});
            var Q95;
            Q95=makeQuery(id+"F5.opExtrude","SWEPT_FACE",FACE,{"disambiguationData":[OSD([sQuery(id+"F4.wireOp",EDGE,"E10.sketch_text.stroke-52")])]});
            var Q96;
            Q96=makeQuery(id+"F5.opExtrude","SWEPT_FACE",FACE,{"disambiguationData":[OSD([sQuery(id+"F4.wireOp",EDGE,"E10.sketch_text.stroke-49")])]});
            var Q97;
            Q97=makeQuery(id+"F5.opExtrude","SWEPT_FACE",FACE,{"disambiguationData":[OSD([sQuery(id+"F4.wireOp",EDGE,"E10.sketch_text.stroke-63")])]});
            var Q98;
            Q98=makeQuery(id+"F5.opExtrude","SWEPT_FACE",FACE,{"disambiguationData":[OSD([sQuery(id+"F4.wireOp",EDGE,"E10.sketch_text.stroke-21")])]});
            var Q99;
            Q99=makeQuery(id+"F5.opExtrude","SWEPT_FACE",FACE,{"disambiguationData":[OSD([sQuery(id+"F4.wireOp",EDGE,"E10.sketch_text.stroke-128")])]});
            var Q100;
            Q100=makeQuery(id+"F5.opExtrude","SWEPT_FACE",FACE,{"disambiguationData":[OSD([sQuery(id+"F4.wireOp",EDGE,"E10.sketch_text.stroke-55")])]});
            var Q101;
            Q101=makeQuery(id+"F5.opExtrude","SWEPT_FACE",FACE,{"disambiguationData":[OSD([sQuery(id+"F4.wireOp",EDGE,"E10.sketch_text.stroke-26")])]});
            var Q102;
            Q102=makeQuery(id+"F5.opExtrude","SWEPT_FACE",FACE,{"disambiguationData":[OSD([sQuery(id+"F4.wireOp",EDGE,"E10.sketch_text.stroke-174")])]});
            var Q103;
            Q103=makeQuery(id+"F5.opExtrude","SWEPT_FACE",FACE,{"disambiguationData":[OSD([sQuery(id+"F4.wireOp",EDGE,"E10.sketch_text.stroke-104")])]});
            var Q104;
            Q104=makeQuery(id+"F5.opExtrude","SWEPT_FACE",FACE,{"disambiguationData":[OSD([sQuery(id+"F4.wireOp",EDGE,"E10.sketch_text.stroke-72")])]});
            var Q105;
            Q105=makeQuery(id+"F5.opExtrude","SWEPT_FACE",FACE,{"disambiguationData":[OSD([sQuery(id+"F4.wireOp",EDGE,"E10.sketch_text.stroke-132")])]});
            var Q106;
            Q106=makeQuery(id+"F5.opExtrude","SWEPT_FACE",FACE,{"disambiguationData":[OSD([sQuery(id+"F4.wireOp",EDGE,"E10.sketch_text.stroke-43")])]});
            var Q107;
            Q107=makeQuery(id+"F5.opExtrude","SWEPT_FACE",FACE,{"disambiguationData":[OSD([sQuery(id+"F4.wireOp",EDGE,"E10.sketch_text.stroke-15")])]});
            var Q108;
            Q108=makeQuery(id+"F5.opExtrude","SWEPT_FACE",FACE,{"disambiguationData":[OSD([sQuery(id+"F4.wireOp",EDGE,"E10.sketch_text.stroke-89")])]});
            var Q109;
            Q109=makeQuery(id+"F5.opExtrude","SWEPT_FACE",FACE,{"disambiguationData":[OSD([sQuery(id+"F4.wireOp",EDGE,"E10.sketch_text.stroke-163")])]});
            var Q110;
            Q110=makeQuery(id+"F5.opExtrude","SWEPT_FACE",FACE,{"disambiguationData":[OSD([sQuery(id+"F4.wireOp",EDGE,"E10.sketch_text.stroke-30")])]});
            var Q111;
            Q111=makeQuery(id+"F5.opExtrude","SWEPT_FACE",FACE,{"disambiguationData":[OSD([sQuery(id+"F4.wireOp",EDGE,"E10.sketch_text.stroke-134")])]});
            var Q112;
            Q112=makeQuery(id+"F5.opExtrude","SWEPT_FACE",FACE,{"disambiguationData":[OSD([sQuery(id+"F4.wireOp",EDGE,"E10.sketch_text.stroke-121")])]});
            var Q113;
            Q113=makeQuery(id+"F5.opExtrude","CAP_FACE",FACE,{"disambiguationData":[OSD([sQuery(id+"F4.wireOp",EDGE,"E10.sketch_text.stroke-105"),sQuery(id+"F4.wireOp",EDGE,"E10.sketch_text.stroke-106"),sQuery(id+"F4.wireOp",EDGE,"E10.sketch_text.stroke-107"),sQuery(id+"F4.wireOp",EDGE,"E10.sketch_text.stroke-108"),sQuery(id+"F4.wireOp",EDGE,"E10.sketch_text.stroke-109"),sQuery(id+"F4.wireOp",EDGE,"E10.sketch_text.stroke-110"),sQuery(id+"F4.wireOp",EDGE,"E10.sketch_text.stroke-111"),sQuery(id+"F4.wireOp",EDGE,"E10.sketch_text.stroke-112"),sQuery(id+"F4.wireOp",EDGE,"E10.sketch_text.stroke-113"),sQuery(id+"F4.wireOp",EDGE,"E10.sketch_text.stroke-114"),sQuery(id+"F4.wireOp",EDGE,"E10.sketch_text.stroke-115"),sQuery(id+"F4.wireOp",EDGE,"E10.sketch_text.stroke-116"),sQuery(id+"F4.wireOp",EDGE,"E10.sketch_text.stroke-117"),sQuery(id+"F4.wireOp",EDGE,"E10.sketch_text.stroke-118"),sQuery(id+"F4.wireOp",EDGE,"E10.sketch_text.stroke-119"),sQuery(id+"F4.wireOp",EDGE,"E10.sketch_text.stroke-120"),sQuery(id+"F4.wireOp",EDGE,"E10.sketch_text.stroke-121"),sQuery(id+"F4.wireOp",EDGE,"E10.sketch_text.stroke-122"),sQuery(id+"F4.wireOp",EDGE,"E10.sketch_text.stroke-123")])],"isStart":false});
            var Q114;
            Q114=makeQuery(id+"F5.opExtrude","SWEPT_FACE",FACE,{"disambiguationData":[OSD([sQuery(id+"F4.wireOp",EDGE,"E10.sketch_text.stroke-92")])]});
            var Q115;
            Q115=makeQuery(id+"F5.opExtrude","SWEPT_FACE",FACE,{"disambiguationData":[OSD([sQuery(id+"F4.wireOp",EDGE,"E10.sketch_text.stroke-46")])]});
            var Q116;
            Q116=makeQuery(id+"F5.opExtrude","CAP_FACE",FACE,{"disambiguationData":[OSD([sQuery(id+"F4.wireOp",EDGE,"E10.sketch_text.stroke-61"),sQuery(id+"F4.wireOp",EDGE,"E10.sketch_text.stroke-62"),sQuery(id+"F4.wireOp",EDGE,"E10.sketch_text.stroke-63"),sQuery(id+"F4.wireOp",EDGE,"E10.sketch_text.stroke-64"),sQuery(id+"F4.wireOp",EDGE,"E10.sketch_text.stroke-65"),sQuery(id+"F4.wireOp",EDGE,"E10.sketch_text.stroke-66"),sQuery(id+"F4.wireOp",EDGE,"E10.sketch_text.stroke-67"),sQuery(id+"F4.wireOp",EDGE,"E10.sketch_text.stroke-68"),sQuery(id+"F4.wireOp",EDGE,"E10.sketch_text.stroke-69"),sQuery(id+"F4.wireOp",EDGE,"E10.sketch_text.stroke-70"),sQuery(id+"F4.wireOp",EDGE,"E10.sketch_text.stroke-71"),sQuery(id+"F4.wireOp",EDGE,"E10.sketch_text.stroke-72"),sQuery(id+"F4.wireOp",EDGE,"E10.sketch_text.stroke-73"),sQuery(id+"F4.wireOp",EDGE,"E10.sketch_text.stroke-74"),sQuery(id+"F4.wireOp",EDGE,"E10.sketch_text.stroke-75"),sQuery(id+"F4.wireOp",EDGE,"E10.sketch_text.stroke-76"),sQuery(id+"F4.wireOp",EDGE,"E10.sketch_text.stroke-77"),sQuery(id+"F4.wireOp",EDGE,"E10.sketch_text.stroke-78"),sQuery(id+"F4.wireOp",EDGE,"E10.sketch_text.stroke-79"),sQuery(id+"F4.wireOp",EDGE,"E10.sketch_text.stroke-80"),sQuery(id+"F4.wireOp",EDGE,"E10.sketch_text.stroke-81"),sQuery(id+"F4.wireOp",EDGE,"E10.sketch_text.stroke-82"),sQuery(id+"F4.wireOp",EDGE,"E10.sketch_text.stroke-83"),sQuery(id+"F4.wireOp",EDGE,"E10.sketch_text.stroke-84"),sQuery(id+"F4.wireOp",EDGE,"E10.sketch_text.stroke-85"),sQuery(id+"F4.wireOp",EDGE,"E10.sketch_text.stroke-86"),sQuery(id+"F4.wireOp",EDGE,"E10.sketch_text.stroke-87"),sQuery(id+"F4.wireOp",EDGE,"E10.sketch_text.stroke-88"),sQuery(id+"F4.wireOp",EDGE,"E10.sketch_text.stroke-89"),sQuery(id+"F4.wireOp",EDGE,"E10.sketch_text.stroke-90"),sQuery(id+"F4.wireOp",EDGE,"E10.sketch_text.stroke-91"),sQuery(id+"F4.wireOp",EDGE,"E10.sketch_text.stroke-92"),sQuery(id+"F4.wireOp",EDGE,"E10.sketch_text.stroke-93"),sQuery(id+"F4.wireOp",EDGE,"E10.sketch_text.stroke-94"),sQuery(id+"F4.wireOp",EDGE,"E10.sketch_text.stroke-95"),sQuery(id+"F4.wireOp",EDGE,"E10.sketch_text.stroke-96"),sQuery(id+"F4.wireOp",EDGE,"E10.sketch_text.stroke-97"),sQuery(id+"F4.wireOp",EDGE,"E10.sketch_text.stroke-98"),sQuery(id+"F4.wireOp",EDGE,"E10.sketch_text.stroke-99"),sQuery(id+"F4.wireOp",EDGE,"E10.sketch_text.stroke-100"),sQuery(id+"F4.wireOp",EDGE,"E10.sketch_text.stroke-101"),sQuery(id+"F4.wireOp",EDGE,"E10.sketch_text.stroke-102"),sQuery(id+"F4.wireOp",EDGE,"E10.sketch_text.stroke-103"),sQuery(id+"F4.wireOp",EDGE,"E10.sketch_text.stroke-104")])],"isStart":false});
            var Q117;
            Q117=makeQuery(id+"F5.opExtrude","SWEPT_FACE",FACE,{"disambiguationData":[OSD([sQuery(id+"F4.wireOp",EDGE,"E10.sketch_text.stroke-33")])]});
            var Q118;
            Q118=makeQuery(id+"F5.opExtrude","SWEPT_FACE",FACE,{"disambiguationData":[OSD([sQuery(id+"F4.wireOp",EDGE,"E10.sketch_text.stroke-93")])]});
            var Q119;
            Q119=makeQuery(id+"F5.opExtrude","SWEPT_FACE",FACE,{"disambiguationData":[OSD([sQuery(id+"F4.wireOp",EDGE,"E10.sketch_text.stroke-34")])]});
            var Q120;
            Q120=makeQuery(id+"F5.opExtrude","SWEPT_FACE",FACE,{"disambiguationData":[OSD([sQuery(id+"F4.wireOp",EDGE,"E10.sketch_text.stroke-152")])]});
            var Q121;
            Q121=makeQuery(id+"F5.opExtrude","SWEPT_FACE",FACE,{"disambiguationData":[OSD([sQuery(id+"F4.wireOp",EDGE,"E10.sketch_text.stroke-51")])]});
            var Q122;
            Q122=makeQuery(id+"F5.opExtrude","SWEPT_FACE",FACE,{"disambiguationData":[OSD([sQuery(id+"F4.wireOp",EDGE,"E10.sketch_text.stroke-6")])]});
            var Q123;
            Q123=makeQuery(id+"F5.opExtrude","SWEPT_FACE",FACE,{"disambiguationData":[OSD([sQuery(id+"F4.wireOp",EDGE,"E10.sketch_text.stroke-7")])]});
            var Q124;
            Q124=makeQuery(id+"F5.opExtrude","SWEPT_FACE",FACE,{"disambiguationData":[OSD([sQuery(id+"F4.wireOp",EDGE,"E10.sketch_text.stroke-156")])]});
            var Q125;
            Q125=makeQuery(id+"F5.opExtrude","SWEPT_FACE",FACE,{"disambiguationData":[OSD([sQuery(id+"F4.wireOp",EDGE,"E10.sketch_text.stroke-112")])]});
            var Q126;
            Q126=makeQuery(id+"F5.boolean.opBoolean","SPLIT",FACE,{"disambiguationData":[TD([makeQuery(id+"F5.opExtrude","SWEPT_FACE",FACE,{"disambiguationData":[OSD([sQuery(id+"F4.wireOp",EDGE,"E10.sketch_text.stroke-182")])]})])],"derivedFrom":makeQuery(id+"F1.opExtrude","CAP_FACE",FACE,{"disambiguationData":[OSD([sQuery(id+"F0.wireOp",EDGE,"E0.bottom"),sQuery(id+"F0.wireOp",EDGE,"E0.top"),sQuery(id+"F0.wireOp",EDGE,"E0.left"),sQuery(id+"F0.wireOp",EDGE,"E0.right"),sQuery(id+"F0.wireOp",EDGE,"E1"),sQuery(id+"F0.wireOp",EDGE,"E7.MirrorC"),sQuery(id+"F0.wireOp",EDGE,"E8.MirrorC"),sQuery(id+"F0.wireOp",EDGE,"E9.MirrorC")])],"isStart":true})});
            var Q127;
            Q127=makeQuery(id+"F5.opExtrude","SWEPT_FACE",FACE,{"disambiguationData":[OSD([sQuery(id+"F4.wireOp",EDGE,"E10.sketch_text.stroke-96")])]});
            var Q128;
            Q128=makeQuery(id+"F5.opExtrude","SWEPT_FACE",FACE,{"disambiguationData":[OSD([sQuery(id+"F4.wireOp",EDGE,"E10.sketch_text.stroke-114")])]});
            var Q129;
            Q129=makeQuery(id+"F5.opExtrude","SWEPT_FACE",FACE,{"disambiguationData":[OSD([sQuery(id+"F4.wireOp",EDGE,"E10.sketch_text.stroke-39")])]});
            var Q130;
            Q130=makeQuery(id+"F5.opExtrude","SWEPT_FACE",FACE,{"disambiguationData":[OSD([sQuery(id+"F4.wireOp",EDGE,"E10.sketch_text.stroke-13")])]});
            var Q131;
            Q131=makeQuery(id+"F5.opExtrude","SWEPT_FACE",FACE,{"disambiguationData":[OSD([sQuery(id+"F4.wireOp",EDGE,"E10.sketch_text.stroke-115")])]});
            var Q132;
            Q132=makeQuery(id+"F5.opExtrude","SWEPT_FACE",FACE,{"disambiguationData":[OSD([sQuery(id+"F4.wireOp",EDGE,"E10.sketch_text.stroke-56")])]});
            var Q133;
            Q133=makeQuery(id+"F5.opExtrude","SWEPT_FACE",FACE,{"disambiguationData":[OSD([sQuery(id+"F4.wireOp",EDGE,"E10.sketch_text.stroke-144")])]});
            var Q134;
            Q134=makeQuery(id+"F5.opExtrude","SWEPT_FACE",FACE,{"disambiguationData":[OSD([sQuery(id+"F4.wireOp",EDGE,"E10.sketch_text.stroke-190")])]});
            var Q135;
            Q135=makeQuery(id+"F5.opExtrude","SWEPT_FACE",FACE,{"disambiguationData":[OSD([sQuery(id+"F4.wireOp",EDGE,"E10.sketch_text.stroke-116")])]});
            var Q136;
            Q136=makeQuery(id+"F5.opExtrude","SWEPT_FACE",FACE,{"disambiguationData":[OSD([sQuery(id+"F4.wireOp",EDGE,"E10.sketch_text.stroke-41")])]});
            var Q137;
            Q137=makeQuery(id+"F5.opExtrude","SWEPT_FACE",FACE,{"disambiguationData":[OSD([sQuery(id+"F4.wireOp",EDGE,"E10.sketch_text.stroke-161")])]});
            var Q138;
            Q138=makeQuery(id+"F5.opExtrude","SWEPT_FACE",FACE,{"disambiguationData":[OSD([sQuery(id+"F4.wireOp",EDGE,"E10.sketch_text.stroke-146")])]});
            var Q139;
            Q139=makeQuery(id+"F5.opExtrude","SWEPT_FACE",FACE,{"disambiguationData":[OSD([sQuery(id+"F4.wireOp",EDGE,"E10.sketch_text.stroke-58")])]});
            var Q140;
            Q140=makeQuery(id+"F5.opExtrude","SWEPT_FACE",FACE,{"disambiguationData":[OSD([sQuery(id+"F4.wireOp",EDGE,"E10.sketch_text.stroke-105")])]});
            var Q141;
            Q141=makeQuery(id+"F5.opExtrude","SWEPT_FACE",FACE,{"disambiguationData":[OSD([sQuery(id+"F4.wireOp",EDGE,"E10.sketch_text.stroke-177")])]});
            var Q142;
            Q142=makeQuery(id+"F5.opExtrude","SWEPT_FACE",FACE,{"disambiguationData":[OSD([sQuery(id+"F4.wireOp",EDGE,"E10.sketch_text.stroke-77")])]});
            var Q143;
            Q143=makeQuery(id+"F5.opExtrude","SWEPT_FACE",FACE,{"disambiguationData":[OSD([sQuery(id+"F4.wireOp",EDGE,"E10.sketch_text.stroke-138")])]});
            var Q144;
            Q144=makeQuery(id+"F5.opExtrude","SWEPT_FACE",FACE,{"disambiguationData":[OSD([sQuery(id+"F4.wireOp",EDGE,"E10.sketch_text.stroke-111")])]});
            var Q145;
            Q145=makeQuery(id+"F5.opExtrude","SWEPT_FACE",FACE,{"disambiguationData":[OSD([sQuery(id+"F4.wireOp",EDGE,"E10.sketch_text.stroke-53")])]});
            var Q146;
            Q146=makeQuery(id+"F5.opExtrude","SWEPT_FACE",FACE,{"disambiguationData":[OSD([sQuery(id+"F4.wireOp",EDGE,"E10.sketch_text.stroke-141")])]});
            var Q147;
            Q147=makeQuery(id+"F5.opExtrude","SWEPT_FACE",FACE,{"disambiguationData":[OSD([sQuery(id+"F4.wireOp",EDGE,"E10.sketch_text.stroke-157")])]});
            var Q148;
            Q148=makeQuery(id+"F5.opExtrude","SWEPT_FACE",FACE,{"disambiguationData":[OSD([sQuery(id+"F4.wireOp",EDGE,"E10.sketch_text.stroke-64")])]});
            var Q149;
            Q149=makeQuery(id+"F5.boolean.opBoolean","SPLIT",FACE,{"disambiguationData":[TD([makeQuery(id+"F5.opExtrude","SWEPT_FACE",FACE,{"disambiguationData":[OSD([sQuery(id+"F4.wireOp",EDGE,"E10.sketch_text.stroke-53")])]})])],"derivedFrom":makeQuery(id+"F1.opExtrude","CAP_FACE",FACE,{"disambiguationData":[OSD([sQuery(id+"F0.wireOp",EDGE,"E0.bottom"),sQuery(id+"F0.wireOp",EDGE,"E0.top"),sQuery(id+"F0.wireOp",EDGE,"E0.left"),sQuery(id+"F0.wireOp",EDGE,"E0.right"),sQuery(id+"F0.wireOp",EDGE,"E1"),sQuery(id+"F0.wireOp",EDGE,"E7.MirrorC"),sQuery(id+"F0.wireOp",EDGE,"E8.MirrorC"),sQuery(id+"F0.wireOp",EDGE,"E9.MirrorC")])],"isStart":true})});
            var Q150;
            Q150=makeQuery(id+"F5.opExtrude","SWEPT_FACE",FACE,{"disambiguationData":[OSD([sQuery(id+"F4.wireOp",EDGE,"E10.sketch_text.stroke-36")])]});
            var Q151;
            Q151=makeQuery(id+"F5.opExtrude","SWEPT_FACE",FACE,{"disambiguationData":[OSD([sQuery(id+"F4.wireOp",EDGE,"E10.sketch_text.stroke-22")])]});
            var Q152;
            Q152=makeQuery(id+"F5.boolean.opBoolean","SPLIT",FACE,{"disambiguationData":[TD([makeQuery(id+"F5.opExtrude","SWEPT_FACE",FACE,{"disambiguationData":[OSD([sQuery(id+"F4.wireOp",EDGE,"E10.sketch_text.stroke-119")])]})])],"derivedFrom":makeQuery(id+"F1.opExtrude","CAP_FACE",FACE,{"disambiguationData":[OSD([sQuery(id+"F0.wireOp",EDGE,"E0.bottom"),sQuery(id+"F0.wireOp",EDGE,"E0.top"),sQuery(id+"F0.wireOp",EDGE,"E0.left"),sQuery(id+"F0.wireOp",EDGE,"E0.right"),sQuery(id+"F0.wireOp",EDGE,"E1"),sQuery(id+"F0.wireOp",EDGE,"E7.MirrorC"),sQuery(id+"F0.wireOp",EDGE,"E8.MirrorC"),sQuery(id+"F0.wireOp",EDGE,"E9.MirrorC")])],"isStart":true})});
            var Q153;
            Q153=makeQuery(id+"F5.boolean.opBoolean","SPLIT",FACE,{"disambiguationData":[TD([makeQuery(id+"F5.opExtrude","SWEPT_FACE",FACE,{"disambiguationData":[OSD([sQuery(id+"F4.wireOp",EDGE,"E10.sketch_text.stroke-158")])]})])],"derivedFrom":makeQuery(id+"F1.opExtrude","CAP_FACE",FACE,{"disambiguationData":[OSD([sQuery(id+"F0.wireOp",EDGE,"E0.bottom"),sQuery(id+"F0.wireOp",EDGE,"E0.top"),sQuery(id+"F0.wireOp",EDGE,"E0.left"),sQuery(id+"F0.wireOp",EDGE,"E0.right"),sQuery(id+"F0.wireOp",EDGE,"E1"),sQuery(id+"F0.wireOp",EDGE,"E7.MirrorC"),sQuery(id+"F0.wireOp",EDGE,"E8.MirrorC"),sQuery(id+"F0.wireOp",EDGE,"E9.MirrorC")])],"isStart":true})});
            var Q154;
            Q154=makeQuery(id+"F5.opExtrude","SWEPT_FACE",FACE,{"disambiguationData":[OSD([sQuery(id+"F4.wireOp",EDGE,"E10.sketch_text.stroke-9")])]});
            var Q155;
            Q155=makeQuery(id+"F5.opExtrude","SWEPT_FACE",FACE,{"disambiguationData":[OSD([sQuery(id+"F4.wireOp",EDGE,"E10.sketch_text.stroke-167")])]});
            var Q156;
            Q156=makeQuery(id+"F5.opExtrude","SWEPT_FACE",FACE,{"disambiguationData":[OSD([sQuery(id+"F4.wireOp",EDGE,"E10.sketch_text.stroke-95")])]});
            var Q157;
            Q157=makeQuery(id+"F5.opExtrude","SWEPT_FACE",FACE,{"disambiguationData":[OSD([sQuery(id+"F4.wireOp",EDGE,"E10.sketch_text.stroke-184")])]});
            var Q158;
            Q158=makeQuery(id+"F5.opExtrude","SWEPT_FACE",FACE,{"disambiguationData":[OSD([sQuery(id+"F4.wireOp",EDGE,"E10.sketch_text.stroke-84")])]});
            var Q159;
            Q159=makeQuery(id+"F5.opExtrude","SWEPT_FACE",FACE,{"disambiguationData":[OSD([sQuery(id+"F4.wireOp",EDGE,"E10.sketch_text.stroke-68")])]});
            var Q160;
            Q160=makeQuery(id+"F5.opExtrude","SWEPT_FACE",FACE,{"disambiguationData":[OSD([sQuery(id+"F4.wireOp",EDGE,"E10.sketch_text.stroke-143")])]});
            var Q161;
            Q161=makeQuery(id+"F5.opExtrude","SWEPT_FACE",FACE,{"disambiguationData":[OSD([sQuery(id+"F4.wireOp",EDGE,"E10.sketch_text.stroke-189")])]});
            var Q162;
            Q162=makeQuery(id+"F5.opExtrude","CAP_FACE",FACE,{"disambiguationData":[OSD([sQuery(id+"F4.wireOp",EDGE,"E10.sketch_text.stroke-13"),sQuery(id+"F4.wireOp",EDGE,"E10.sketch_text.stroke-14"),sQuery(id+"F4.wireOp",EDGE,"E10.sketch_text.stroke-15"),sQuery(id+"F4.wireOp",EDGE,"E10.sketch_text.stroke-16"),sQuery(id+"F4.wireOp",EDGE,"E10.sketch_text.stroke-17"),sQuery(id+"F4.wireOp",EDGE,"E10.sketch_text.stroke-18"),sQuery(id+"F4.wireOp",EDGE,"E10.sketch_text.stroke-19"),sQuery(id+"F4.wireOp",EDGE,"E10.sketch_text.stroke-20")])],"isStart":false});
            var Q163;
            Q163=makeQuery(id+"F5.opExtrude","SWEPT_FACE",FACE,{"disambiguationData":[OSD([sQuery(id+"F4.wireOp",EDGE,"E10.sketch_text.stroke-57")])]});
            var Q164;
            Q164=makeQuery(id+"F5.opExtrude","SWEPT_FACE",FACE,{"disambiguationData":[OSD([sQuery(id+"F4.wireOp",EDGE,"E10.sketch_text.stroke-29")])]});
            var Q165;
            Q165=makeQuery(id+"F5.opExtrude","SWEPT_FACE",FACE,{"disambiguationData":[OSD([sQuery(id+"F4.wireOp",EDGE,"E10.sketch_text.stroke-60")])]});
            var Q166;
            Q166=makeQuery(id+"F5.opExtrude","SWEPT_FACE",FACE,{"disambiguationData":[OSD([sQuery(id+"F4.wireOp",EDGE,"E10.sketch_text.stroke-148")])]});
            var Q167;
            Q167=makeQuery(id+"F5.opExtrude","SWEPT_FACE",FACE,{"disambiguationData":[OSD([sQuery(id+"F4.wireOp",EDGE,"E10.sketch_text.stroke-75")])]});
            var Q168;
            Q168=makeQuery(id+"F5.opExtrude","SWEPT_FACE",FACE,{"disambiguationData":[OSD([sQuery(id+"F4.wireOp",EDGE,"E10.sketch_text.stroke-91")])]});
            var Q169;
            Q169=makeQuery(id+"F5.opExtrude","SWEPT_FACE",FACE,{"disambiguationData":[OSD([sQuery(id+"F4.wireOp",EDGE,"E10.sketch_text.stroke-78")])]});
            var Q170;
            Q170=makeQuery(id+"F5.opExtrude","SWEPT_FACE",FACE,{"disambiguationData":[OSD([sQuery(id+"F4.wireOp",EDGE,"E10.sketch_text.stroke-62")])]});
            var Q171;
            Q171=makeQuery(id+"F5.opExtrude","SWEPT_FACE",FACE,{"disambiguationData":[OSD([sQuery(id+"F4.wireOp",EDGE,"E10.sketch_text.stroke-182")])]});
            var Q172;
            Q172=makeQuery(id+"F5.opExtrude","SWEPT_FACE",FACE,{"disambiguationData":[OSD([sQuery(id+"F4.wireOp",EDGE,"E10.sketch_text.stroke-11")])]});
            var Q173;
            Q173=makeQuery(id+"F5.opExtrude","SWEPT_FACE",FACE,{"disambiguationData":[OSD([sQuery(id+"F4.wireOp",EDGE,"E10.sketch_text.stroke-97")])]});
            var Q174;
            Q174=makeQuery(id+"F5.opExtrude","SWEPT_FACE",FACE,{"disambiguationData":[OSD([sQuery(id+"F4.wireOp",EDGE,"E10.sketch_text.stroke-23")])]});
            var Q175;
            Q175=makeQuery(id+"F5.opExtrude","SWEPT_FACE",FACE,{"disambiguationData":[OSD([sQuery(id+"F4.wireOp",EDGE,"E10.sketch_text.stroke-80")])]});
            var Q176;
            Q176=makeQuery(id+"F5.boolean.opBoolean","SPLIT",FACE,{"disambiguationData":[TD([makeQuery(id+"F5.opExtrude","SWEPT_FACE",FACE,{"disambiguationData":[OSD([sQuery(id+"F4.wireOp",EDGE,"E10.sketch_text.stroke-99")])]})])],"derivedFrom":makeQuery(id+"F1.opExtrude","CAP_FACE",FACE,{"disambiguationData":[OSD([sQuery(id+"F0.wireOp",EDGE,"E0.bottom"),sQuery(id+"F0.wireOp",EDGE,"E0.top"),sQuery(id+"F0.wireOp",EDGE,"E0.left"),sQuery(id+"F0.wireOp",EDGE,"E0.right"),sQuery(id+"F0.wireOp",EDGE,"E1"),sQuery(id+"F0.wireOp",EDGE,"E7.MirrorC"),sQuery(id+"F0.wireOp",EDGE,"E8.MirrorC"),sQuery(id+"F0.wireOp",EDGE,"E9.MirrorC")])],"isStart":true})});
            var Q177;
            Q177=makeQuery(id+"F5.opExtrude","SWEPT_FACE",FACE,{"disambiguationData":[OSD([sQuery(id+"F4.wireOp",EDGE,"E10.sketch_text.stroke-168")])]});
            var Q178;
            Q178=makeQuery(id+"F5.opExtrude","SWEPT_FACE",FACE,{"disambiguationData":[OSD([sQuery(id+"F4.wireOp",EDGE,"E10.sketch_text.stroke-188")])]});
            var Q179;
            Q179=makeQuery(id+"F5.opExtrude","SWEPT_FACE",FACE,{"disambiguationData":[OSD([sQuery(id+"F4.wireOp",EDGE,"E10.sketch_text.stroke-129")])]});
            var Q180;
            Q180=makeQuery(id+"F5.opExtrude","SWEPT_FACE",FACE,{"disambiguationData":[OSD([sQuery(id+"F4.wireOp",EDGE,"E10.sketch_text.stroke-27")])]});
            var Q181;
            Q181=makeQuery(id+"F5.opExtrude","SWEPT_FACE",FACE,{"disambiguationData":[OSD([sQuery(id+"F4.wireOp",EDGE,"E10.sketch_text.stroke-175")])]});
            var Q182;
            Q182=makeQuery(id+"F5.opExtrude","SWEPT_FACE",FACE,{"disambiguationData":[OSD([sQuery(id+"F4.wireOp",EDGE,"E10.sketch_text.stroke-42")])]});
            var Q183;
            Q183=makeQuery(id+"F5.opExtrude","SWEPT_FACE",FACE,{"disambiguationData":[OSD([sQuery(id+"F4.wireOp",EDGE,"E10.sketch_text.stroke-118")])]});
            var Q184;
            Q184=makeQuery(id+"F5.opExtrude","SWEPT_FACE",FACE,{"disambiguationData":[OSD([sQuery(id+"F4.wireOp",EDGE,"E10.sketch_text.stroke-151")])]});
            var Q185;
            Q185=makeQuery(id+"F5.opExtrude","SWEPT_FACE",FACE,{"disambiguationData":[OSD([sQuery(id+"F4.wireOp",EDGE,"E10.sketch_text.stroke-137")])]});
            var Q186;
            Q186=makeQuery(id+"F5.opExtrude","SWEPT_FACE",FACE,{"disambiguationData":[OSD([sQuery(id+"F4.wireOp",EDGE,"E10.sketch_text.stroke-83")])]});
            var Q187;
            Q187=makeQuery(id+"F5.boolean.opBoolean","SPLIT",FACE,{"disambiguationData":[TD([makeQuery(id+"F5.opExtrude","SWEPT_FACE",FACE,{"disambiguationData":[OSD([sQuery(id+"F4.wireOp",EDGE,"E10.sketch_text.stroke-90")])]})])],"derivedFrom":makeQuery(id+"F1.opExtrude","CAP_FACE",FACE,{"disambiguationData":[OSD([sQuery(id+"F0.wireOp",EDGE,"E0.bottom"),sQuery(id+"F0.wireOp",EDGE,"E0.top"),sQuery(id+"F0.wireOp",EDGE,"E0.left"),sQuery(id+"F0.wireOp",EDGE,"E0.right"),sQuery(id+"F0.wireOp",EDGE,"E1"),sQuery(id+"F0.wireOp",EDGE,"E7.MirrorC"),sQuery(id+"F0.wireOp",EDGE,"E8.MirrorC"),sQuery(id+"F0.wireOp",EDGE,"E9.MirrorC")])],"isStart":true})});
            var Q188;
            Q188=makeQuery(id+"F5.opExtrude","SWEPT_FACE",FACE,{"disambiguationData":[OSD([sQuery(id+"F4.wireOp",EDGE,"E10.sketch_text.stroke-139")])]});
            var Q189;
            Q189=makeQuery(id+"F5.opExtrude","SWEPT_FACE",FACE,{"disambiguationData":[OSD([sQuery(id+"F4.wireOp",EDGE,"E10.sketch_text.stroke-70")])]});
            var Q190;
            Q190=makeQuery(id+"F5.opExtrude","SWEPT_FACE",FACE,{"disambiguationData":[OSD([sQuery(id+"F4.wireOp",EDGE,"E10.sketch_text.stroke-160")])]});
            var Q191;
            Q191=makeQuery(id+"F5.opExtrude","SWEPT_FACE",FACE,{"disambiguationData":[OSD([sQuery(id+"F4.wireOp",EDGE,"E10.sketch_text.stroke-71")])]});
            var Q192;
            Q192=makeQuery(id+"F5.opExtrude","SWEPT_FACE",FACE,{"disambiguationData":[OSD([sQuery(id+"F4.wireOp",EDGE,"E10.sketch_text.stroke-117")])]});
            var Q193;
            Q193=makeQuery(id+"F5.opExtrude","SWEPT_FACE",FACE,{"disambiguationData":[OSD([sQuery(id+"F4.wireOp",EDGE,"E10.sketch_text.stroke-147")])]});
            var Q194;
            Q194=makeQuery(id+"F5.opExtrude","SWEPT_FACE",FACE,{"disambiguationData":[OSD([sQuery(id+"F4.wireOp",EDGE,"E10.sketch_text.stroke-164")])]});
            var Q195;
            Q195=makeQuery(id+"F5.opExtrude","SWEPT_FACE",FACE,{"disambiguationData":[OSD([sQuery(id+"F4.wireOp",EDGE,"E10.sketch_text.stroke-61")])]});
            var Q196;
            Q196=makeQuery(id+"F5.opExtrude","SWEPT_FACE",FACE,{"disambiguationData":[OSD([sQuery(id+"F4.wireOp",EDGE,"E10.sketch_text.stroke-19")])]});
            var Q197;
            Q197=makeQuery(id+"F5.opExtrude","SWEPT_FACE",FACE,{"disambiguationData":[OSD([sQuery(id+"F4.wireOp",EDGE,"E10.sketch_text.stroke-35")])]});
            var Q198;
            Q198=makeQuery(id+"F5.opExtrude","SWEPT_FACE",FACE,{"disambiguationData":[OSD([sQuery(id+"F4.wireOp",EDGE,"E10.sketch_text.stroke-140")])]});
            var Q199;
            Q199=makeQuery(id+"F5.opExtrude","SWEPT_FACE",FACE,{"disambiguationData":[OSD([sQuery(id+"F4.wireOp",EDGE,"E10.sketch_text.stroke-20")])]});
            var Q200;
            Q200=makeQuery(id+"F5.opExtrude","SWEPT_FACE",FACE,{"disambiguationData":[OSD([sQuery(id+"F4.wireOp",EDGE,"E10.sketch_text.stroke-16")])]});
            var Q201;
            Q201=makeQuery(id+"F5.opExtrude","SWEPT_FACE",FACE,{"disambiguationData":[OSD([sQuery(id+"F4.wireOp",EDGE,"E10.sketch_text.stroke-18")])]});
            var Q202;
            Q202=makeQuery(id+"F5.opExtrude","SWEPT_FACE",FACE,{"disambiguationData":[OSD([sQuery(id+"F4.wireOp",EDGE,"E10.sketch_text.stroke-17")])]});
            var Q203;
            Q203=qCreatedBy(makeId("Right.planeOp"),FACE);
            mirror(context, id + "F6", {"operationType" : NewBodyOperationType.ADD, "entities" : qUnion([Q0]), "faces" : qUnion([Q1, Q2, Q3, Q4, Q5, Q6, Q7, Q8, Q9, Q10, Q11, Q12, Q13, Q14, Q15, Q16, Q17, Q18, Q19, Q20, Q21, Q22, Q23, Q24, Q25, Q26, Q27, Q28, Q29, Q30, Q31, Q32, Q33, Q34, Q35, Q36, Q37, Q38, Q39, Q40, Q41, Q42, Q43, Q44, Q45, Q46, Q47, Q48, Q49, Q50, Q51, Q52, Q53, Q54, Q55, Q56, Q57, Q58, Q59, Q60, Q61, Q62, Q63, Q64, Q65, Q66, Q67, Q68, Q69, Q70, Q71, Q72, Q73, Q74, Q75, Q76, Q77, Q78, Q79, Q80, Q81, Q82, Q83, Q84, Q85, Q86, Q87, Q88, Q89, Q90, Q91, Q92, Q93, Q94, Q95, Q96, Q97, Q98, Q99, Q100, Q101, Q102, Q103, Q104, Q105, Q106, Q107, Q108, Q109, Q110, Q111, Q112, Q113, Q114, Q115, Q116, Q117, Q118, Q119, Q120, Q121, Q122, Q123, Q124, Q125, Q126, Q127, Q128, Q129, Q130, Q131, Q132, Q133, Q134, Q135, Q136, Q137, Q138, Q139, Q140, Q141, Q142, Q143, Q144, Q145, Q146, Q147, Q148, Q149, Q150, Q151, Q152, Q153, Q154, Q155, Q156, Q157, Q158, Q159, Q160, Q161, Q162, Q163, Q164, Q165, Q166, Q167, Q168, Q169, Q170, Q171, Q172, Q173, Q174, Q175, Q176, Q177, Q178, Q179, Q180, Q181, Q182, Q183, Q184, Q185, Q186, Q187, Q188, Q189, Q190, Q191, Q192, Q193, Q194, Q195, Q196, Q197, Q198, Q199, Q200, Q201, Q202]), "mirrorPlane" : qUnion([Q203])});
        }
    });
